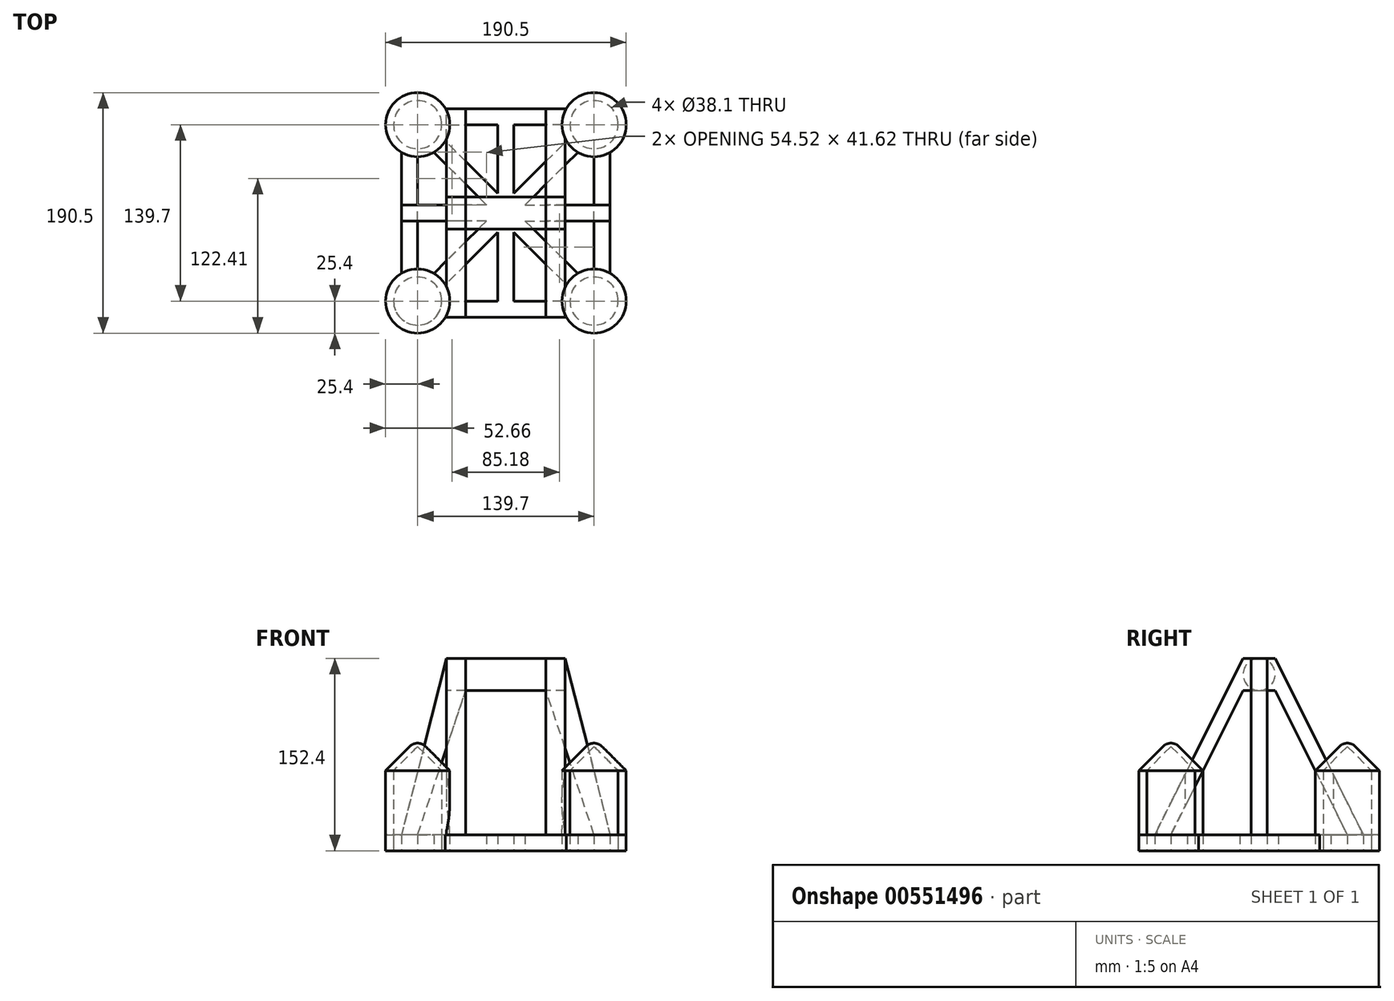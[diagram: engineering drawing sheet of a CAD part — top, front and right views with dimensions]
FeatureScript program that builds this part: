
annotation { "Feature Type Name" : "Feature", "Feature Type Description" : "" }
export const myFeature = defineFeature(function(context is Context, id is Id, definition is map)
    precondition{}
    {
        {
            var Q0;
            Q0=qCreatedBy(makeId("Top.planeOp"),FACE);
            var sketch = newSketch(context, id + "F0", { "sketchPlane" : qUnion([Q0])});
            skCircle(sketch, "E0", {"center": v(69.85, 69.85) * mm, "radius": 19.05 * mm});
            skArc(sketch, "E1", {"start": v(82.55, 47.85) * mm, "mid": v(87.81, 87.81) * mm, "end": v(47.85, 82.55) * mm});
            skLineSegment(sketch, "E2", {"start": v(82.55, 6.35) * mm, "end": v(82.55, 47.85) * mm});
            skLineSegment(sketch, "E3", {"start": v(82.55, 0) * mm, "end": v(82.55, 6.35) * mm});
            skLineSegment(sketch, "E4", {"start": v(0, 82.55) * mm, "end": v(47.85, 82.55) * mm});
            skLineSegment(sketch, "E5", {"start": v(6.35, 69.85) * mm, "end": v(6.35, 15.33) * mm});
            skLineSegment(sketch, "E6", {"start": v(6.35, 15.33) * mm, "end": v(47.97, 56.95) * mm});
            skLineSegment(sketch, "E7", {"start": v(15.33, 6.35) * mm, "end": v(56.95, 47.97) * mm});
            skPoint(sketch, "E8.orphan", {"position": v(6.35, 0) * mm});
            skLineSegment(sketch, "E9.trimOffspring", {"start": v(44.45, 69.85) * mm, "end": v(6.35, 69.85) * mm});
            skArc(sketch, "E10.trimOffspring", {"start": v(44.45, 69.85) * mm, "mid": v(45.35, 63.16) * mm, "end": v(47.97, 56.95) * mm});
            skLineSegment(sketch, "E11", {"start": v(69.85, 44.45) * mm, "end": v(69.85, 6.35) * mm});
            skLineSegment(sketch, "E12", {"start": v(15.33, 6.35) * mm, "end": v(69.85, 6.35) * mm});
            skLineSegment(sketch, "E13.MirrorCS", {"start": v(82.55, 0) * mm, "end": v(82.55, -6.35) * mm});
            skLineSegment(sketch, "E14.MirrorCS", {"start": v(15.33, -6.35) * mm, "end": v(69.85, -6.35) * mm});
            skLineSegment(sketch, "E15.MirrorCS", {"start": v(44.45, -69.85) * mm, "end": v(6.35, -69.85) * mm});
            skLineSegment(sketch, "E16.MirrorCS", {"start": v(69.85, -44.45) * mm, "end": v(69.85, -6.35) * mm});
            skLineSegment(sketch, "E17.MirrorCS", {"start": v(6.35, -69.85) * mm, "end": v(6.35, -15.33) * mm});
            skLineSegment(sketch, "E18.MirrorCS", {"start": v(6.35, -15.33) * mm, "end": v(47.97, -56.95) * mm});
            skLineSegment(sketch, "E19.MirrorCS", {"start": v(15.33, -6.35) * mm, "end": v(56.95, -47.97) * mm});
            skArc(sketch, "E20.MirrorCS", {"start": v(44.45, -69.85) * mm, "mid": v(45.35, -63.16) * mm, "end": v(47.97, -56.95) * mm});
            skLineSegment(sketch, "E21.MirrorCS", {"start": v(0, -82.55) * mm, "end": v(47.85, -82.55) * mm});
            skArc(sketch, "E22.MirrorCS", {"start": v(82.55, -47.85) * mm, "mid": v(87.81, -87.81) * mm, "end": v(47.85, -82.55) * mm});
            skLineSegment(sketch, "E23.MirrorCS", {"start": v(82.55, -6.35) * mm, "end": v(82.55, -47.85) * mm});
            skCircle(sketch, "E24.MirrorC", {"center": v(69.85, -69.85) * mm, "radius": 19.05 * mm});
            skLineSegment(sketch, "E25.MirrorCS", {"start": v(-82.55, 0) * mm, "end": v(-82.55, 6.35) * mm});
            skLineSegment(sketch, "E26.MirrorCS", {"start": v(-82.55, 0) * mm, "end": v(-82.55, -6.35) * mm});
            skPoint(sketch, "E27.MirrorP", {"position": v(-6.35, 0) * mm});
            skLineSegment(sketch, "E28.MirrorCS", {"start": v(-15.33, -6.35) * mm, "end": v(-56.95, -47.97) * mm});
            skLineSegment(sketch, "E29.MirrorCS", {"start": v(-6.35, 15.33) * mm, "end": v(-47.97, 56.95) * mm});
            skLineSegment(sketch, "E30.MirrorCS", {"start": v(-15.33, 6.35) * mm, "end": v(-56.95, 47.97) * mm});
            skArc(sketch, "E31.MirrorCS", {"start": v(-44.45, 69.85) * mm, "mid": v(-45.35, 63.16) * mm, "end": v(-47.97, 56.95) * mm});
            skCircle(sketch, "E32.MirrorC", {"center": v(-69.85, 69.85) * mm, "radius": 19.05 * mm});
            skArc(sketch, "E33.MirrorCS", {"start": v(-44.45, -69.85) * mm, "mid": v(-45.35, -63.16) * mm, "end": v(-47.97, -56.95) * mm});
            skLineSegment(sketch, "E34.MirrorCS", {"start": v(-6.35, -69.85) * mm, "end": v(-6.35, -15.33) * mm});
            skLineSegment(sketch, "E35.MirrorCS", {"start": v(-82.55, -6.35) * mm, "end": v(-82.55, -47.85) * mm});
            skLineSegment(sketch, "E36.MirrorCS", {"start": v(0, -82.55) * mm, "end": v(-47.85, -82.55) * mm});
            skLineSegment(sketch, "E37.MirrorCS", {"start": v(-44.45, 69.85) * mm, "end": v(-6.35, 69.85) * mm});
            skArc(sketch, "E38.MirrorCS", {"start": v(-82.55, 47.85) * mm, "mid": v(-87.81, 87.81) * mm, "end": v(-47.85, 82.55) * mm});
            skLineSegment(sketch, "E39.MirrorCS", {"start": v(-6.35, 69.85) * mm, "end": v(-6.35, 15.33) * mm});
            skLineSegment(sketch, "E40.MirrorCS", {"start": v(-15.33, 6.35) * mm, "end": v(-69.85, 6.35) * mm});
            skLineSegment(sketch, "E41.MirrorCS", {"start": v(-44.45, -69.85) * mm, "end": v(-6.35, -69.85) * mm});
            skLineSegment(sketch, "E42.MirrorCS", {"start": v(-69.85, 44.45) * mm, "end": v(-69.85, 6.35) * mm});
            skCircle(sketch, "E43.MirrorC", {"center": v(-69.85, -69.85) * mm, "radius": 19.05 * mm});
            skLineSegment(sketch, "E44.MirrorCS", {"start": v(-15.33, -6.35) * mm, "end": v(-69.85, -6.35) * mm});
            skLineSegment(sketch, "E45.MirrorCS", {"start": v(-6.35, -15.33) * mm, "end": v(-47.97, -56.95) * mm});
            skLineSegment(sketch, "E46.MirrorCS", {"start": v(0, 82.55) * mm, "end": v(-47.85, 82.55) * mm});
            skLineSegment(sketch, "E47.MirrorCS", {"start": v(-82.55, 6.35) * mm, "end": v(-82.55, 47.85) * mm});
            skArc(sketch, "E48.MirrorCS", {"start": v(-82.55, -47.85) * mm, "mid": v(-87.81, -87.81) * mm, "end": v(-47.85, -82.55) * mm});
            skLineSegment(sketch, "E49.MirrorCS", {"start": v(-69.85, -44.45) * mm, "end": v(-69.85, -6.35) * mm});
            skArc(sketch, "E50.trimOffspring", {"start": v(56.95, -47.97) * mm, "mid": v(63.16, -45.35) * mm, "end": v(69.85, -44.45) * mm});
            skArc(sketch, "E51.trimOffspring", {"start": v(-56.95, -47.97) * mm, "mid": v(-63.16, -45.35) * mm, "end": v(-69.85, -44.45) * mm});
            skPoint(sketch, "E52.orphan", {"position": v(69.85, 0) * mm});
            skArc(sketch, "E53.trimOffspring", {"start": v(-56.95, 47.97) * mm, "mid": v(-63.16, 45.35) * mm, "end": v(-69.85, 44.45) * mm});
            skArc(sketch, "E54.trimOffspring", {"start": v(56.95, 47.97) * mm, "mid": v(63.16, 45.35) * mm, "end": v(69.85, 44.45) * mm});
            skPoint(sketch, "E55.start.orphan", {"position": v(0, 69.85) * mm});
            skSolve(sketch);
        }
        {
            var Q0;
            Q0=makeQuery(id+"F0.imprint","IMPRINT",FACE,{"disambiguationData":[TD([[makeQuery(id+"F0.imprint","IMPRINT",EDGE,{"derivedFrom":sQuery(id+"F0.wireOp",EDGE,"E0")}),-1.0]])]});
            extrude(context, id + "F1", {"entities" : qUnion([Q0]), "depth" : 12.7 * mm, "offsetDistance" : 25.4 * mm});
        }
        {
            var Q0;
            Q0=makeQuery(id+"F1.opExtrude","CAP_FACE",FACE,{"disambiguationData":[OSD([sQuery(id+"F0.wireOp",EDGE,"E0"),sQuery(id+"F0.wireOp",EDGE,"E1"),sQuery(id+"F0.wireOp",EDGE,"E2"),sQuery(id+"F0.wireOp",EDGE,"E3"),sQuery(id+"F0.wireOp",EDGE,"E4"),sQuery(id+"F0.wireOp",EDGE,"E5"),sQuery(id+"F0.wireOp",EDGE,"E6"),sQuery(id+"F0.wireOp",EDGE,"E7"),sQuery(id+"F0.wireOp",EDGE,"E9.trimOffspring"),sQuery(id+"F0.wireOp",EDGE,"E10.trimOffspring"),sQuery(id+"F0.wireOp",EDGE,"E11"),sQuery(id+"F0.wireOp",EDGE,"E12"),sQuery(id+"F0.wireOp",EDGE,"E13.MirrorCS"),sQuery(id+"F0.wireOp",EDGE,"E14.MirrorCS"),sQuery(id+"F0.wireOp",EDGE,"E15.MirrorCS"),sQuery(id+"F0.wireOp",EDGE,"E16.MirrorCS"),sQuery(id+"F0.wireOp",EDGE,"E17.MirrorCS"),sQuery(id+"F0.wireOp",EDGE,"E18.MirrorCS"),sQuery(id+"F0.wireOp",EDGE,"E19.MirrorCS"),sQuery(id+"F0.wireOp",EDGE,"E20.MirrorCS"),sQuery(id+"F0.wireOp",EDGE,"E21.MirrorCS"),sQuery(id+"F0.wireOp",EDGE,"E22.MirrorCS"),sQuery(id+"F0.wireOp",EDGE,"E23.MirrorCS"),sQuery(id+"F0.wireOp",EDGE,"E24.MirrorC"),sQuery(id+"F0.wireOp",EDGE,"E25.MirrorCS"),sQuery(id+"F0.wireOp",EDGE,"E26.MirrorCS"),sQuery(id+"F0.wireOp",EDGE,"E28.MirrorCS"),sQuery(id+"F0.wireOp",EDGE,"E29.MirrorCS"),sQuery(id+"F0.wireOp",EDGE,"E30.MirrorCS"),sQuery(id+"F0.wireOp",EDGE,"E31.MirrorCS"),sQuery(id+"F0.wireOp",EDGE,"E32.MirrorC"),sQuery(id+"F0.wireOp",EDGE,"E33.MirrorCS"),sQuery(id+"F0.wireOp",EDGE,"E34.MirrorCS"),sQuery(id+"F0.wireOp",EDGE,"E35.MirrorCS"),sQuery(id+"F0.wireOp",EDGE,"E36.MirrorCS"),sQuery(id+"F0.wireOp",EDGE,"E37.MirrorCS"),sQuery(id+"F0.wireOp",EDGE,"E38.MirrorCS"),sQuery(id+"F0.wireOp",EDGE,"E39.MirrorCS"),sQuery(id+"F0.wireOp",EDGE,"E40.MirrorCS"),sQuery(id+"F0.wireOp",EDGE,"E41.MirrorCS"),sQuery(id+"F0.wireOp",EDGE,"E42.MirrorCS"),sQuery(id+"F0.wireOp",EDGE,"E43.MirrorC"),sQuery(id+"F0.wireOp",EDGE,"E44.MirrorCS"),sQuery(id+"F0.wireOp",EDGE,"E45.MirrorCS"),sQuery(id+"F0.wireOp",EDGE,"E46.MirrorCS"),sQuery(id+"F0.wireOp",EDGE,"E47.MirrorCS"),sQuery(id+"F0.wireOp",EDGE,"E48.MirrorCS"),sQuery(id+"F0.wireOp",EDGE,"E49.MirrorCS"),sQuery(id+"F0.wireOp",EDGE,"E50.trimOffspring"),sQuery(id+"F0.wireOp",EDGE,"E51.trimOffspring"),sQuery(id+"F0.wireOp",EDGE,"E53.trimOffspring"),sQuery(id+"F0.wireOp",EDGE,"E54.trimOffspring")])],"isStart":false});
            var sketch = newSketch(context, id + "F2", { "sketchPlane" : qUnion([Q0])});
            skCircle(sketch, "E56.0", {"center": v(-69.85, 69.85) * mm, "radius": 19.05 * mm});
            skCircle(sketch, "E57.0", {"center": v(69.85, 69.85) * mm, "radius": 19.05 * mm});
            skCircle(sketch, "E58.0", {"center": v(69.85, -69.85) * mm, "radius": 19.05 * mm});
            skCircle(sketch, "E59.0", {"center": v(-69.85, -69.85) * mm, "radius": 19.05 * mm});
            skArc(sketch, "E60.0", {"start": v(-82.55, 47.85) * mm, "mid": v(-87.81, 87.81) * mm, "end": v(-47.85, 82.55) * mm});
            skArc(sketch, "E61.0", {"start": v(82.55, 47.85) * mm, "mid": v(87.81, 87.81) * mm, "end": v(47.85, 82.55) * mm});
            skArc(sketch, "E62.0", {"start": v(-82.55, -47.85) * mm, "mid": v(-87.81, -87.81) * mm, "end": v(-47.85, -82.55) * mm});
            skArc(sketch, "E63.0", {"start": v(82.55, -47.85) * mm, "mid": v(87.81, -87.81) * mm, "end": v(47.85, -82.55) * mm});
            skCircle(sketch, "E64", {"center": v(-69.85, 69.85) * mm, "radius": 25.4 * mm});
            skCircle(sketch, "E65", {"center": v(69.85, 69.85) * mm, "radius": 25.4 * mm});
            skCircle(sketch, "E66", {"center": v(69.85, -69.85) * mm, "radius": 25.4 * mm});
            skCircle(sketch, "E67", {"center": v(-69.85, -69.85) * mm, "radius": 25.4 * mm});
            skSolve(sketch);
        }
        {
            var Q0;
            Q0=makeQuery(id+"F2.imprint","IMPRINT",FACE,{"disambiguationData":[TD([[makeQuery(id+"F2.imprint","IMPRINT",EDGE,{"derivedFrom":sQuery(id+"F2.wireOp",EDGE,"E56.0")}),1.0]])]});
            var Q1;
            Q1=makeQuery(id+"F2.imprint","IMPRINT",FACE,{"disambiguationData":[TD([[makeQuery(id+"F2.imprint","IMPRINT",EDGE,{"derivedFrom":sQuery(id+"F2.wireOp",EDGE,"E59.0")}),-1.0]])]});
            var Q2;
            Q2=makeQuery(id+"F2.imprint","IMPRINT",FACE,{"disambiguationData":[TD([[makeQuery(id+"F2.imprint","IMPRINT",EDGE,{"derivedFrom":sQuery(id+"F2.wireOp",EDGE,"E58.0")}),1.0]])]});
            var Q3;
            Q3=makeQuery(id+"F2.imprint","IMPRINT",FACE,{"disambiguationData":[TD([[makeQuery(id+"F2.imprint","IMPRINT",EDGE,{"derivedFrom":sQuery(id+"F2.wireOp",EDGE,"E57.0")}),-1.0]])]});
            extrude(context, id + "F3", {"entities" : qUnion([Q0, Q1, Q2, Q3]), "operationType" : NewBodyOperationType.ADD, "depth" : 50.8 * mm, "offsetDistance" : 25.4 * mm});
        }
        {
            var Q0;
            Q0=qCreatedBy(makeId("Right.planeOp"),FACE);
            var sketch = newSketch(context, id + "F4", { "sketchPlane" : qUnion([Q0])});
            skLineSegment(sketch, "E68", {"start": v(0, 0) * mm, "end": v(0, 139.7) * mm});
            skCircle(sketch, "E69", {"center": v(0, 139.7) * mm, "radius": 12.7 * mm});
            skSolve(sketch);
        }
        {
            var Q0;
            Q0=makeQuery(id+"F4.imprint","IMPRINT",FACE,{"disambiguationData":[TD([[makeQuery(id+"F4.imprint","IMPRINT",EDGE,{"derivedFrom":sQuery(id+"F4.wireOp",EDGE,"E69")}),1.0]])]});
            extrude(context, id + "F5", {"entities" : qUnion([Q0]), "endBound" : BoundingType.SYMMETRIC, "depth" : 63.5 * mm, "offsetDistance" : 25.4 * mm});
        }
        {
            var Q0;
            Q0=makeQuery(id+"F5.opExtrude","CAP_FACE",FACE,{"disambiguationData":[OSD([sQuery(id+"F4.wireOp",EDGE,"E69")])],"isStart":true});
            var sketch = newSketch(context, id + "F6", { "sketchPlane" : qUnion([Q0])});
            skCircle(sketch, "E70.0", {"center": v(0, 139.7) * mm, "radius": 12.7 * mm});
            skLineSegment(sketch, "E71", {"start": v(0, 139.7) * mm, "end": v(-12.7, 139.7) * mm});
            skLineSegment(sketch, "E72", {"start": v(-12.7, 139.7) * mm, "end": v(-12.7, 152.4) * mm});
            skLineSegment(sketch, "E73", {"start": v(-12.7, 152.4) * mm, "end": v(12.7, 152.4) * mm});
            skLineSegment(sketch, "E74", {"start": v(12.7, 152.4) * mm, "end": v(12.7, 127) * mm});
            skLineSegment(sketch, "E75", {"start": v(12.7, 127) * mm, "end": v(-12.7, 127) * mm});
            skLineSegment(sketch, "E76", {"start": v(-12.7, 127) * mm, "end": v(-12.7, 139.7) * mm});
            skSolve(sketch);
        }
        {
            var Q0;
            {var subQ0=sQuery(id+"F6.wireOp",EDGE,"E74");var subQ1=sQuery(id+"F6.wireOp",EDGE,"E70.0");var subQ2=makeQuery(id+"F6.imprint","INTERSECT",VERTEX,{"derivedFrom":[subQ1,subQ0]});Q0=makeQuery(id+"F6.imprint","IMPRINT",FACE,{"disambiguationData":[TD([[makeQuery(id+"F6.imprint","IMPRINT",EDGE,{"disambiguationData":[TD([[subQ2,-1.0]])],"derivedFrom":subQ1}),1.0]])]});}
            var Q1;
            {var subQ0=sQuery(id+"F6.wireOp",EDGE,"E70.0");var subQ2=makeQuery(id+"F6.imprint","INTERSECT",VERTEX,{"derivedFrom":[subQ0,sQuery(id+"F6.wireOp",EDGE,"E73")]});Q1=makeQuery(id+"F6.imprint","IMPRINT",FACE,{"disambiguationData":[TD([[makeQuery(id+"F6.imprint","IMPRINT",EDGE,{"disambiguationData":[TD([[subQ2,-1.0]])],"derivedFrom":subQ0}),-1.0]])]});}
            var Q2;
            {var subQ0=sQuery(id+"F6.wireOp",EDGE,"E76");Q2=makeQuery(id+"F6.imprint","IMPRINT",FACE,{"disambiguationData":[TD([[makeQuery(id+"F6.imprint","IMPRINT",EDGE,{"derivedFrom":subQ0}),-1.0]])]});}
            var Q3;
            {var subQ0=sQuery(id+"F6.wireOp",EDGE,"E73");var subQ1=sQuery(id+"F6.wireOp",EDGE,"E70.0");var subQ2=makeQuery(id+"F6.imprint","INTERSECT",VERTEX,{"derivedFrom":[subQ1,subQ0]});Q3=makeQuery(id+"F6.imprint","IMPRINT",FACE,{"disambiguationData":[TD([[makeQuery(id+"F6.imprint","IMPRINT",EDGE,{"disambiguationData":[TD([[subQ2,-1.0]])],"derivedFrom":subQ1}),1.0]])]});}
            var Q4;
            {var subQ0=sQuery(id+"F6.wireOp",EDGE,"E72");Q4=makeQuery(id+"F6.imprint","IMPRINT",FACE,{"disambiguationData":[TD([[makeQuery(id+"F6.imprint","IMPRINT",EDGE,{"derivedFrom":subQ0}),-1.0]])]});}
            extrude(context, id + "F7", {"entities" : qUnion([Q0, Q1, Q2, Q3, Q4]), "depth" : 12.7 * mm, "offsetDistance" : 25.4 * mm});
        }
        {
            var Q0;
            Q0=makeQuery(id+"F7.opExtrude","SWEPT_BODY",BODY,{"disambiguationData":[OSD([sQuery(id+"F6.wireOp",EDGE,"E72"),sQuery(id+"F6.wireOp",EDGE,"E73"),sQuery(id+"F6.wireOp",EDGE,"E74"),sQuery(id+"F6.wireOp",EDGE,"E75"),sQuery(id+"F6.wireOp",EDGE,"E76")])]});
            var Q1;
            Q1=qCreatedBy(makeId("Right.planeOp"),FACE);
            mirror(context, id + "F8", {"operationType" : NewBodyOperationType.ADD, "entities" : qUnion([Q0]), "mirrorPlane" : qUnion([Q1])});
        }
        {
            var Q0;
            Q0=qCreatedBy(makeId("Front.planeOp"),FACE);
            cPlane(context, id + "F9", {"entities" : qUnion([Q0]), "cplaneType" : CPlaneType.OFFSET, "offset" : 69.85 * mm, "width" : 152.4 * mm, "height" : 152.4 * mm});
        }
        {
            var Q0;
            Q0=qCreatedBy(id+"F9.planeOp",FACE);
            var sketch = newSketch(context, id + "F10", { "sketchPlane" : qUnion([Q0])});
            skLineSegment(sketch, "E77.0", {"start": v(-95.25, 63.5) * mm, "end": v(-44.45, 63.5) * mm});
            skLineSegment(sketch, "E78.0", {"start": v(-88.9, 63.5) * mm, "end": v(-50.8, 63.5) * mm});
            skLineSegment(sketch, "E79", {"start": v(-69.85, 82.55) * mm, "end": v(-88.9, 63.5) * mm});
            skLineSegment(sketch, "E80", {"start": v(-95.25, 63.5) * mm, "end": v(-76.2, 82.55) * mm});
            skPoint(sketch, "E81.orphan", {"position": v(-65.9, 82.55) * mm});
            skArc(sketch, "E82", {"start": v(-69.85, 85.18) * mm, "mid": v(-73.29, 84.5) * mm, "end": v(-76.2, 82.55) * mm});
            skLineSegment(sketch, "E83", {"start": v(-69.85, 82.55) * mm, "end": v(-69.85, 85.18) * mm});
            skPoint(sketch, "E84.orphan", {"position": v(-63.5, 82.55) * mm});
            skPoint(sketch, "E85.start.orphan", {"position": v(-69.85, 63.5) * mm});
            skSolve(sketch);
        }
        {
            var Q0;
            {var subQ1=sQuery(id+"F10.wireOp",EDGE,"E79");Q0=makeQuery(id+"F10.imprint","IMPRINT",FACE,{"disambiguationData":[TD([[makeQuery(id+"F10.imprint","IMPRINT",EDGE,{"derivedFrom":subQ1}),-1.0]])]});}
            var Q1;
            Q1=makeQuery(id+"F3.opExtrude","CAP_EDGE",EDGE,{"disambiguationData":[OSD([sQuery(id+"F2.wireOp",EDGE,"E59.0")])],"isStart":false});
            revolve(context, id + "F11", {"entities" : qUnion([Q0]), "axis" : qUnion([Q1]), "revolveType" : RevolveType.FULL});
        }
        {
            var Q0;
            Q0=makeQuery(id+"F11.opRevolve","SWEPT_BODY",BODY,{"disambiguationData":[OSD([sQuery(id+"F10.wireOp",EDGE,"E77.0"),sQuery(id+"F10.wireOp",EDGE,"E79"),sQuery(id+"F10.wireOp",EDGE,"E80"),sQuery(id+"F10.wireOp",EDGE,"E82"),sQuery(id+"F10.wireOp",EDGE,"E83")])]});
            var Q1;
            Q1=qCreatedBy(makeId("Front.planeOp"),FACE);
            mirror(context, id + "F12", {"entities" : qUnion([Q0]), "mirrorPlane" : qUnion([Q1])});
        }
        {
            var Q0;
            Q0=makeQuery(id+"F11.opRevolve","SWEPT_BODY",BODY,{"disambiguationData":[OSD([sQuery(id+"F10.wireOp",EDGE,"E77.0"),sQuery(id+"F10.wireOp",EDGE,"E79"),sQuery(id+"F10.wireOp",EDGE,"E80"),sQuery(id+"F10.wireOp",EDGE,"E82"),sQuery(id+"F10.wireOp",EDGE,"E83")])]});
            var Q1;
            Q1=makeQuery(id+"F12.opPattern","COPY",BODY,{"derivedFrom":makeQuery(id+"F11.opRevolve","SWEPT_BODY",BODY,{"disambiguationData":[OSD([sQuery(id+"F10.wireOp",EDGE,"E77.0"),sQuery(id+"F10.wireOp",EDGE,"E79"),sQuery(id+"F10.wireOp",EDGE,"E80"),sQuery(id+"F10.wireOp",EDGE,"E82"),sQuery(id+"F10.wireOp",EDGE,"E83")])]}),"instanceName":"1"});
            var Q2;
            Q2=qCreatedBy(makeId("Right.planeOp"),FACE);
            mirror(context, id + "F13", {"operationType" : NewBodyOperationType.ADD, "entities" : qUnion([Q0, Q1]), "mirrorPlane" : qUnion([Q2])});
        }
        {
            var Q0;
            Q0=makeQuery(id+"F7.opExtrude","CAP_FACE",FACE,{"disambiguationData":[OSD([sQuery(id+"F6.wireOp",EDGE,"E72"),sQuery(id+"F6.wireOp",EDGE,"E73"),sQuery(id+"F6.wireOp",EDGE,"E74"),sQuery(id+"F6.wireOp",EDGE,"E75"),sQuery(id+"F6.wireOp",EDGE,"E76")])],"isStart":false});
            var sketch = newSketch(context, id + "F14", { "sketchPlane" : qUnion([Q0])});
            skPoint(sketch, "E86.0", {"position": v(69.85, 12.7) * mm});
            skPoint(sketch, "E87.0", {"position": v(12.7, 127) * mm});
            skLineSegment(sketch, "E88", {"start": v(12.7, 127) * mm, "end": v(69.85, 12.7) * mm});
            skPoint(sketch, "E89.0", {"position": v(12.7, 152.4) * mm});
            skLineSegment(sketch, "E90", {"start": v(12.7, 152.4) * mm, "end": v(82.55, 12.7) * mm});
            skLineSegment(sketch, "E91", {"start": v(69.85, 12.7) * mm, "end": v(82.55, 12.7) * mm});
            skLineSegment(sketch, "E92", {"start": v(12.7, 127) * mm, "end": v(12.7, 152.4) * mm});
            skSolve(sketch);
        }
        {
            var Q0;
            Q0=makeQuery(id+"F14.imprint","IMPRINT",FACE,{"disambiguationData":[TD([[makeQuery(id+"F14.imprint","IMPRINT",EDGE,{"derivedFrom":sQuery(id+"F14.wireOp",EDGE,"E88")}),1.0]])]});
            extrude(context, id + "F15", {"entities" : qUnion([Q0]), "depth" : 2.54 * mm, "offsetDistance" : 25.4 * mm, "hasSecondDirection" : true, "secondDirectionOppositeDirection" : true, "secondDirectionDepth" : 12.7 * mm});
        }
        {
            var Q0;
            Q0=makeQuery(id+"F15.opExtrude","SWEPT_BODY",BODY,{"disambiguationData":[OSD([sQuery(id+"F14.wireOp",EDGE,"E88"),sQuery(id+"F14.wireOp",EDGE,"E90"),sQuery(id+"F14.wireOp",EDGE,"E91"),sQuery(id+"F14.wireOp",EDGE,"E92")])]});
            var Q1;
            Q1=qCreatedBy(makeId("Right.planeOp"),FACE);
            mirror(context, id + "F16", {"entities" : qUnion([Q0]), "mirrorPlane" : qUnion([Q1])});
        }
        {
            var Q0;
            Q0=makeQuery(id+"F15.opExtrude","SWEPT_BODY",BODY,{"disambiguationData":[OSD([sQuery(id+"F14.wireOp",EDGE,"E88"),sQuery(id+"F14.wireOp",EDGE,"E90"),sQuery(id+"F14.wireOp",EDGE,"E91"),sQuery(id+"F14.wireOp",EDGE,"E92")])]});
            var Q1;
            Q1=makeQuery(id+"F16.opPattern","COPY",BODY,{"derivedFrom":makeQuery(id+"F15.opExtrude","SWEPT_BODY",BODY,{"disambiguationData":[OSD([sQuery(id+"F14.wireOp",EDGE,"E88"),sQuery(id+"F14.wireOp",EDGE,"E90"),sQuery(id+"F14.wireOp",EDGE,"E91"),sQuery(id+"F14.wireOp",EDGE,"E92")])]}),"instanceName":"1"});
            var Q2;
            Q2=qCreatedBy(makeId("Front.planeOp"),FACE);
            mirror(context, id + "F17", {"operationType" : NewBodyOperationType.ADD, "entities" : qUnion([Q0, Q1]), "mirrorPlane" : qUnion([Q2])});
        }
        {
            var Q0;
            Q0=makeQuery(id+"F7.opExtrude","CAP_FACE",FACE,{"disambiguationData":[OSD([sQuery(id+"F6.wireOp",EDGE,"E72"),sQuery(id+"F6.wireOp",EDGE,"E73"),sQuery(id+"F6.wireOp",EDGE,"E74"),sQuery(id+"F6.wireOp",EDGE,"E75"),sQuery(id+"F6.wireOp",EDGE,"E76")])],"isStart":false});
            var sketch = newSketch(context, id + "F18", { "sketchPlane" : qUnion([Q0])});
            skLineSegment(sketch, "E93.0.0", {"start": v(12.7, 127) * mm, "end": v(12.7, 152.4) * mm});
            skLineSegment(sketch, "E93.0.1", {"start": v(12.7, 152.4) * mm, "end": v(-12.7, 152.4) * mm});
            skLineSegment(sketch, "E93.0.2", {"start": v(-12.7, 152.4) * mm, "end": v(-12.7, 127) * mm});
            skLineSegment(sketch, "E93.0.3", {"start": v(-12.7, 127) * mm, "end": v(12.7, 127) * mm});
            skSolve(sketch);
        }
        {
            var Q0;
            Q0=makeQuery(id+"F18.imprint","IMPRINT",FACE,{"disambiguationData":[TD([[makeQuery(id+"F18.imprint","IMPRINT",EDGE,{"derivedFrom":sQuery(id+"F18.wireOp",EDGE,"E93.0.0")}),-1.0]])]});
            extrude(context, id + "F19", {"entities" : qUnion([Q0]), "depth" : 2.54 * mm, "offsetDistance" : 25.4 * mm});
        }
        {
            var Q0;
            Q0=makeQuery(id+"F19.opExtrude","SWEPT_BODY",BODY,{"disambiguationData":[OSD([sQuery(id+"F18.wireOp",EDGE,"E93.0.0"),sQuery(id+"F18.wireOp",EDGE,"E93.0.1"),sQuery(id+"F18.wireOp",EDGE,"E93.0.2"),sQuery(id+"F18.wireOp",EDGE,"E93.0.3")])]});
            var Q1;
            Q1=qCreatedBy(makeId("Right.planeOp"),FACE);
            mirror(context, id + "F20", {"operationType" : NewBodyOperationType.ADD, "entities" : qUnion([Q0]), "mirrorPlane" : qUnion([Q1])});
        }
        {
            var Q0;
            Q0=qCreatedBy(makeId("Front.planeOp"),FACE);
            var sketch = newSketch(context, id + "F21", { "sketchPlane" : qUnion([Q0])});
            skLineSegment(sketch, "E94.0", {"start": v(-47, 152.4) * mm, "end": v(-31.75, 152.4) * mm});
            skPoint(sketch, "E95.0", {"position": v(-82.55, 12.7) * mm});
            skLineSegment(sketch, "E96.0.0", {"start": v(-6.35, 12.7) * mm, "end": v(-31.75, 12.7) * mm});
            skLineSegment(sketch, "E96.0.2", {"start": v(-31.75, 12.7) * mm, "end": v(31.75, 12.7) * mm});
            skLineSegment(sketch, "E96.0.4", {"start": v(31.75, 12.7) * mm, "end": v(6.35, 12.7) * mm});
            skLineSegment(sketch, "E96.0.6", {"start": v(6.35, 12.7) * mm, "end": v(47.97, 12.7) * mm});
            skLineSegment(sketch, "E96.0.7", {"start": v(47.97, 12.7) * mm, "end": v(56.95, 12.7) * mm});
            skLineSegment(sketch, "E96.0.8", {"start": v(56.95, 12.7) * mm, "end": v(15.33, 12.7) * mm});
            skLineSegment(sketch, "E96.0.9", {"start": v(15.33, 12.7) * mm, "end": v(69.85, 12.7) * mm});
            skLineSegment(sketch, "E96.0.11", {"start": v(69.85, 12.7) * mm, "end": v(82.55, 12.7) * mm});
            skLineSegment(sketch, "E96.0.13", {"start": v(82.55, 12.7) * mm, "end": v(69.85, 12.7) * mm});
            skLineSegment(sketch, "E96.0.15", {"start": v(69.85, 12.7) * mm, "end": v(15.33, 12.7) * mm});
            skLineSegment(sketch, "E96.0.16", {"start": v(15.33, 12.7) * mm, "end": v(56.95, 12.7) * mm});
            skLineSegment(sketch, "E96.0.17", {"start": v(56.95, 12.7) * mm, "end": v(47.97, 12.7) * mm});
            skLineSegment(sketch, "E96.0.18", {"start": v(47.97, 12.7) * mm, "end": v(6.35, 12.7) * mm});
            skLineSegment(sketch, "E96.0.20", {"start": v(6.35, 12.7) * mm, "end": v(31.75, 12.7) * mm});
            skLineSegment(sketch, "E96.0.22", {"start": v(31.75, 12.7) * mm, "end": v(-31.75, 12.7) * mm});
            skLineSegment(sketch, "E96.0.24", {"start": v(-31.75, 12.7) * mm, "end": v(-6.35, 12.7) * mm});
            skLineSegment(sketch, "E96.0.26", {"start": v(-6.35, 12.7) * mm, "end": v(-47.97, 12.7) * mm});
            skLineSegment(sketch, "E96.0.27", {"start": v(-47.97, 12.7) * mm, "end": v(-56.95, 12.7) * mm});
            skLineSegment(sketch, "E96.0.28", {"start": v(-56.95, 12.7) * mm, "end": v(-15.33, 12.7) * mm});
            skLineSegment(sketch, "E96.0.29", {"start": v(-15.33, 12.7) * mm, "end": v(-69.85, 12.7) * mm});
            skLineSegment(sketch, "E96.0.31", {"start": v(-69.85, 12.7) * mm, "end": v(-82.55, 12.7) * mm});
            skLineSegment(sketch, "E96.0.33", {"start": v(-82.55, 12.7) * mm, "end": v(-69.85, 12.7) * mm});
            skLineSegment(sketch, "E96.0.35", {"start": v(-69.85, 12.7) * mm, "end": v(-15.33, 12.7) * mm});
            skLineSegment(sketch, "E96.0.36", {"start": v(-15.33, 12.7) * mm, "end": v(-56.95, 12.7) * mm});
            skLineSegment(sketch, "E96.0.37", {"start": v(-56.95, 12.7) * mm, "end": v(-47.97, 12.7) * mm});
            skLineSegment(sketch, "E96.0.38", {"start": v(-47.97, 12.7) * mm, "end": v(-6.35, 12.7) * mm});
            skPoint(sketch, "E97.0", {"position": v(-47, 127) * mm});
            skLineSegment(sketch, "E98", {"start": v(-47, 152.4) * mm, "end": v(-82.55, 12.7) * mm});
            skPoint(sketch, "E99.0", {"position": v(-31.75, 127) * mm});
            skLineSegment(sketch, "E100", {"start": v(-69.85, 12.7) * mm, "end": v(-31.75, 127) * mm});
            skLineSegment(sketch, "E101", {"start": v(-31.75, 127) * mm, "end": v(-31.75, 152.4) * mm});
            skSolve(sketch);
        }
        {
            var Q0;
            Q0=makeQuery(id+"F21.imprint","IMPRINT",FACE,{"disambiguationData":[TD([[makeQuery(id+"F21.imprint","IMPRINT",EDGE,{"derivedFrom":sQuery(id+"F21.wireOp",EDGE,"E94.0")}),-1.0]])]});
            extrude(context, id + "F22", {"entities" : qUnion([Q0]), "endBound" : BoundingType.SYMMETRIC, "depth" : 12.7 * mm, "offsetDistance" : 25.4 * mm});
        }
        {
            var Q0;
            Q0=makeQuery(id+"F22.opExtrude","SWEPT_BODY",BODY,{"disambiguationData":[OSD([sQuery(id+"F21.wireOp",EDGE,"E94.0"),sQuery(id+"F21.wireOp",EDGE,"E98"),sQuery(id+"F21.wireOp",EDGE,"E100"),sQuery(id+"F21.wireOp",EDGE,"E101"),sQuery(id+"F21.wireOp",EDGE,"E96.0.33")])]});
            var Q1;
            Q1=qCreatedBy(makeId("Right.planeOp"),FACE);
            mirror(context, id + "F23", {"operationType" : NewBodyOperationType.ADD, "entities" : qUnion([Q0]), "mirrorPlane" : qUnion([Q1])});
        }
    });
